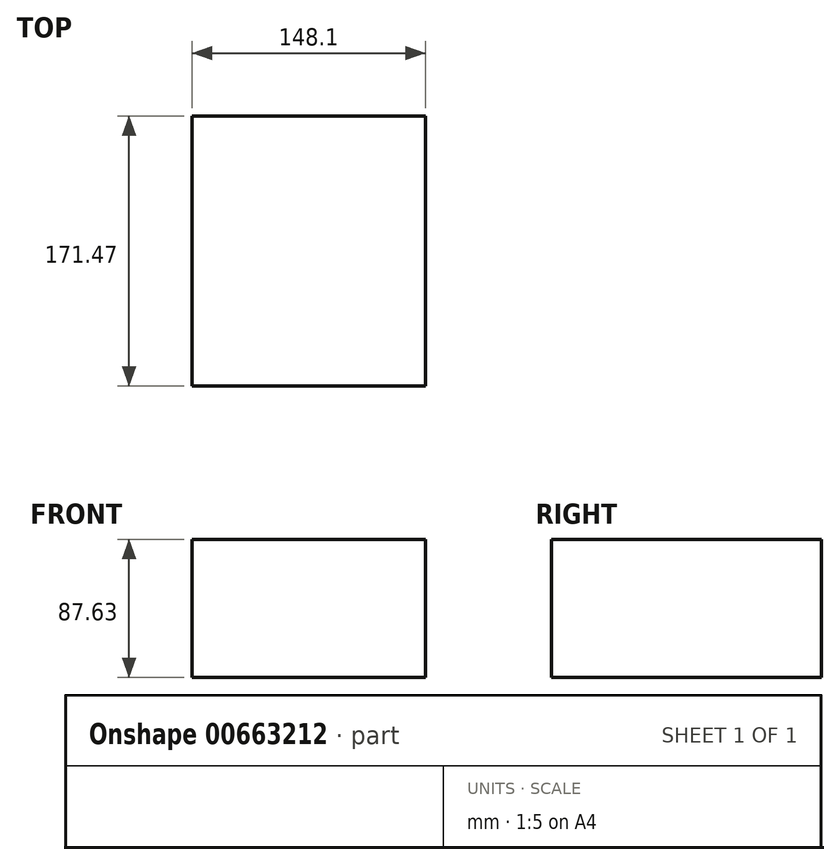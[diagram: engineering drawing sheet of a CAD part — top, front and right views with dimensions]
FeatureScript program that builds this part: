
annotation { "Feature Type Name" : "Feature", "Feature Type Description" : "" }
export const myFeature = defineFeature(function(context is Context, id is Id, definition is map)
    precondition{}
    {
        {
            var Q0;
            Q0=qCreatedBy(makeId("Top.planeOp"),FACE);
            var sketch = newSketch(context, id + "F0", { "sketchPlane" : qUnion([Q0])});
            skLineSegment(sketch, "E0.bottom", {"start": v(41.15, 84.76) * mm, "end": v(-106.95, 84.76) * mm});
            skLineSegment(sketch, "E0.top", {"start": v(41.15, -86.71) * mm, "end": v(-106.95, -86.71) * mm});
            skLineSegment(sketch, "E0.left", {"start": v(41.15, 84.76) * mm, "end": v(41.15, -86.71) * mm});
            skLineSegment(sketch, "E0.right", {"start": v(-106.95, 84.76) * mm, "end": v(-106.95, -86.71) * mm});
            skSolve(sketch);
        }
        {
            var Q0;
            Q0=makeQuery(id+"F0.imprint","IMPRINT",FACE,{"disambiguationData":[TD([[makeQuery(id+"F0.imprint","IMPRINT",EDGE,{"derivedFrom":sQuery(id+"F0.wireOp",EDGE,"E0.bottom")}),1.0]])]});
            extrude(context, id + "F1", {"entities" : qUnion([Q0]), "depth" : 87.63 * mm, "offsetDistance" : 25.4 * mm});
        }
    });
